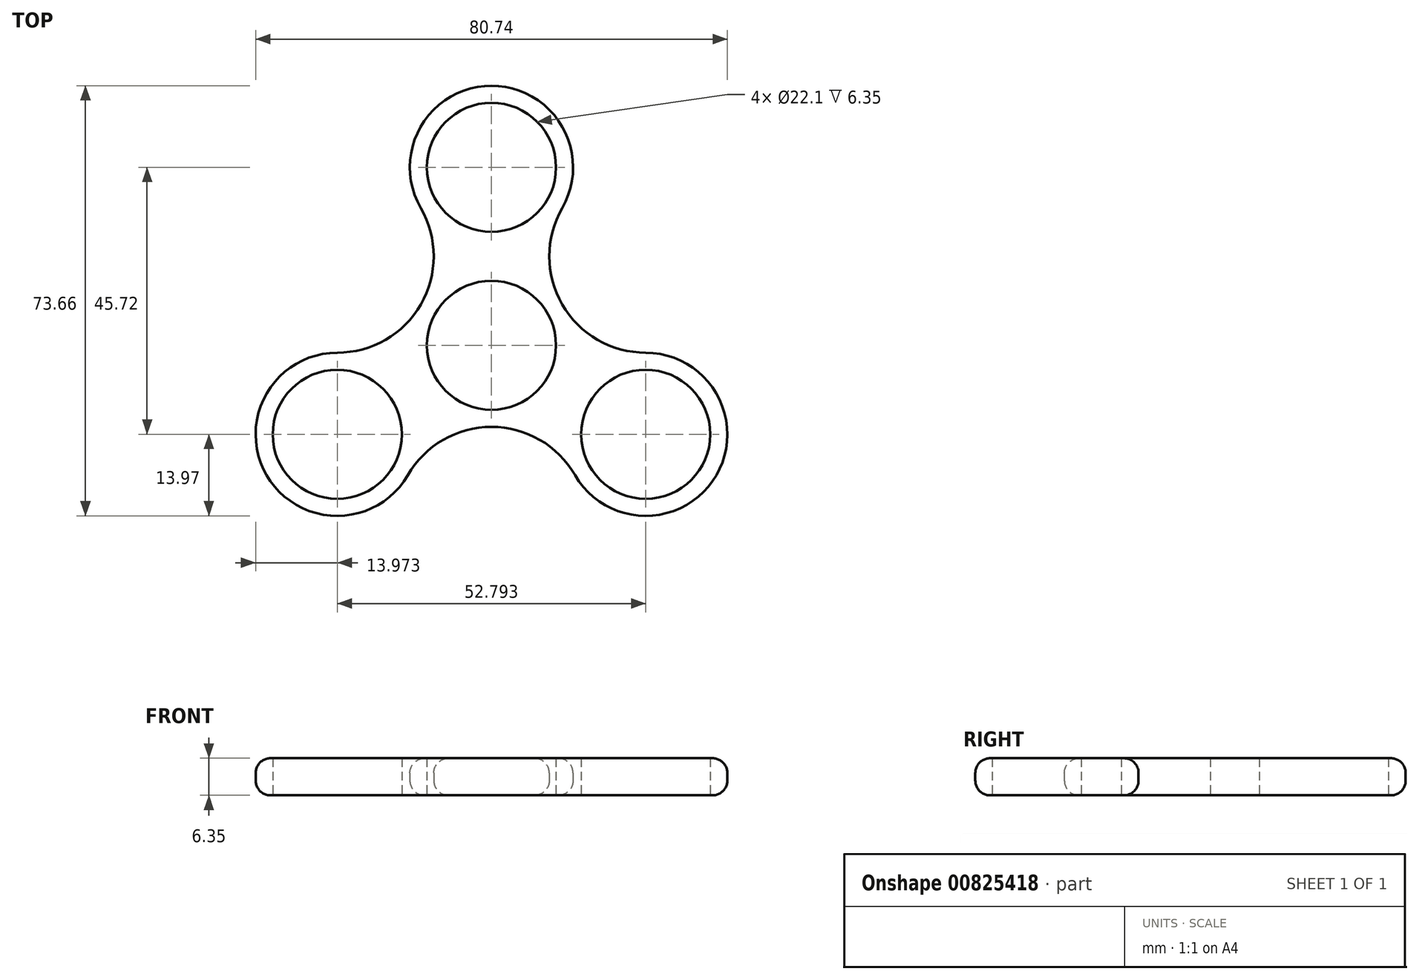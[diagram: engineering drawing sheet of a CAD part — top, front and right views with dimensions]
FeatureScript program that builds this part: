
annotation { "Feature Type Name" : "Feature", "Feature Type Description" : "" }
export const myFeature = defineFeature(function(context is Context, id is Id, definition is map)
    precondition{}
    {
        {
            var Q0;
            Q0=qCreatedBy(makeId("Top.planeOp"),FACE);
            var sketch = newSketch(context, id + "F0", { "sketchPlane" : qUnion([Q0])});
            skCircle(sketch, "E0", {"center": v(0, 0) * mm, "radius": 11.05 * mm});
            skCircle(sketch, "E1", {"center": v(0, 0) * mm, "radius": 13.97 * mm});
            skLineSegment(sketch, "E2", {"start": v(0, 0) * mm, "end": v(0, 30.48) * mm});
            skCircle(sketch, "E3", {"center": v(0, 30.48) * mm, "radius": 11.05 * mm});
            skArc(sketch, "E4", {"start": v(11, 21.86) * mm, "mid": v(0, 44.45) * mm, "end": v(-11, 21.86) * mm});
            skCircle(sketch, "E5.1.0", {"center": v(-26.4, -15.24) * mm, "radius": 11.05 * mm});
            skArc(sketch, "E5.1.1", {"start": v(-24.43, -1.4) * mm, "mid": v(-38.5, -22.22) * mm, "end": v(-13.43, -20.45) * mm});
            skCircle(sketch, "E5.2.0", {"center": v(26.4, -15.24) * mm, "radius": 11.05 * mm});
            skArc(sketch, "E5.2.1", {"start": v(13.43, -20.45) * mm, "mid": v(38.5, -22.23) * mm, "end": v(24.43, -1.4) * mm});
            skLineSegment(sketch, "E6", {"start": v(0, 0) * mm, "end": v(-26.4, 15.24) * mm});
            skArc(sketch, "E7", {"start": v(-26.4, -1.27) * mm, "mid": v(-12.1, 6.99) * mm, "end": v(-12.1, 23.5) * mm});
            skArc(sketch, "E8.1.0", {"start": v(14.3, -22.23) * mm, "mid": v(0, -13.97) * mm, "end": v(-14.3, -22.22) * mm});
            skArc(sketch, "E8.2.0", {"start": v(12.1, 23.5) * mm, "mid": v(12.1, 6.98) * mm, "end": v(26.4, -1.27) * mm});
            skSolve(sketch);
        }
        {
            var Q0;
            Q0 = qSketchRegion(id + "F0", true);
            extrude(context, id + "F1", {"entities" : qUnion([Q0]), "depth" : 6.35 * mm, "offsetDistance" : 25.4 * mm});
        }
        {
            var Q0;
            Q0=makeQuery(id+"F1.opExtrude","CAP_EDGE",EDGE,{"disambiguationData":[OSD([sQuery(id+"F0.wireOp",EDGE,"E8.1.0")])],"isStart":false});
            var Q1;
            Q1=makeQuery(id+"F1.opExtrude","CAP_EDGE",EDGE,{"disambiguationData":[OSD([sQuery(id+"F0.wireOp",EDGE,"E8.1.0")])],"isStart":true});
            fillet(context, id + "F2", {"entities" : qUnion([Q0, Q1]), "radius" : 2.54 * mm, "tangentPropagation" : true, "allowEdgeOverflow" : false});
        }
    });
